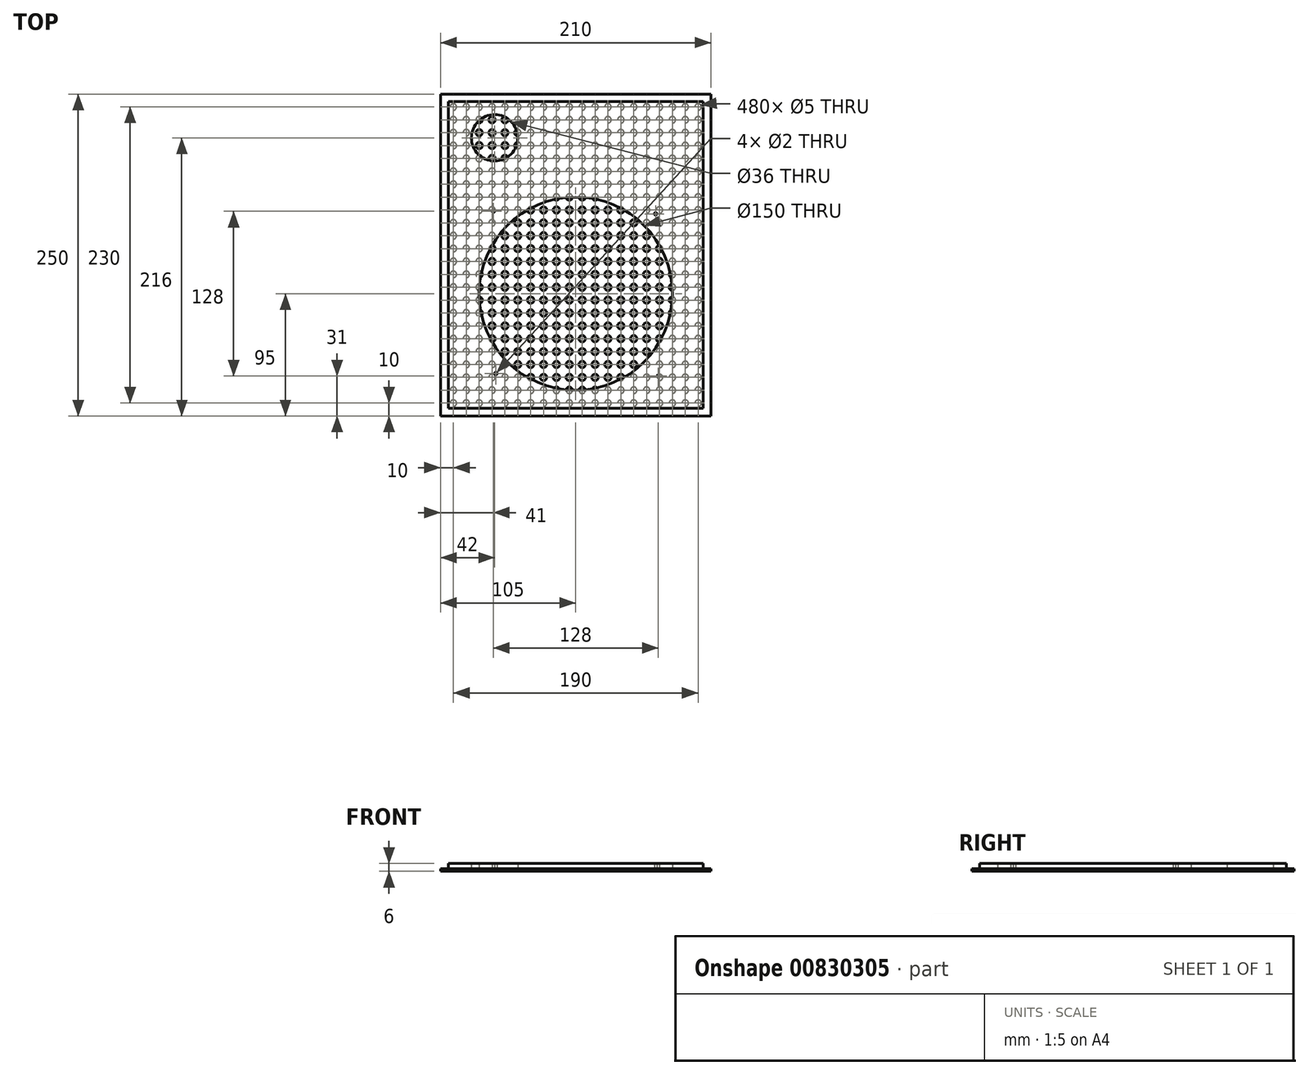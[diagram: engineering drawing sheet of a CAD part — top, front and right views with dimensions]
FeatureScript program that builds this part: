
annotation { "Feature Type Name" : "Feature", "Feature Type Description" : "" }
export const myFeature = defineFeature(function(context is Context, id is Id, definition is map)
    precondition{}
    {
        {
            var Q0;
            Q0=qCreatedBy(makeId("Top.planeOp"),FACE);
            var sketch = newSketch(context, id + "F0", { "sketchPlane" : qUnion([Q0])});
            skLineSegment(sketch, "E0.bottom", {"start": v(99, 119) * mm, "end": v(-99, 119) * mm});
            skLineSegment(sketch, "E0.top", {"start": v(99, -119) * mm, "end": v(-99, -119) * mm});
            skLineSegment(sketch, "E0.left", {"start": v(99, 119) * mm, "end": v(99, -119) * mm});
            skLineSegment(sketch, "E0.right", {"start": v(-99, 119) * mm, "end": v(-99, -119) * mm});
            skPoint(sketch, "E0.middle", {"position": v(0, 0) * mm});
            skSolve(sketch);
        }
        {
            var Q0;
            Q0=makeQuery(id+"F0.imprint","IMPRINT",FACE,{"disambiguationData":[TD([[makeQuery(id+"F0.imprint","IMPRINT",EDGE,{"derivedFrom":sQuery(id+"F0.wireOp",EDGE,"E0.bottom")}),1.0]])]});
            var sketch = newSketch(context, id + "F1", { "sketchPlane" : qUnion([Q0])});
            skCircle(sketch, "E1", {"center": v(0, -30) * mm, "radius": 75 * mm});
            skCircle(sketch, "E2", {"center": v(-63, 91) * mm, "radius": 18 * mm});
            skCircle(sketch, "E3", {"center": v(-64, 34) * mm, "radius": 1 * mm});
            skCircle(sketch, "E4", {"center": v(61.98, 31.98) * mm, "radius": 1 * mm});
            skCircle(sketch, "E5", {"center": v(64, -94) * mm, "radius": 1 * mm});
            skCircle(sketch, "E6", {"center": v(-61.98, -91.98) * mm, "radius": 1 * mm});
            skSolve(sketch);
        }
        {
            var Q0;
            Q0=qCreatedBy(makeId("Top.planeOp"),FACE);
            var sketch = newSketch(context, id + "F2", { "sketchPlane" : qUnion([Q0])});
            skLineSegment(sketch, "E7.bottom", {"start": v(-105, 125) * mm, "end": v(105, 125) * mm});
            skLineSegment(sketch, "E7.top", {"start": v(-105, -125) * mm, "end": v(105, -125) * mm});
            skLineSegment(sketch, "E7.left", {"start": v(-105, 125) * mm, "end": v(-105, -125) * mm});
            skLineSegment(sketch, "E7.right", {"start": v(105, 125) * mm, "end": v(105, -125) * mm});
            skPoint(sketch, "E7.middle", {"position": v(0, 0) * mm});
            skCircle(sketch, "E8", {"center": v(95, -115) * mm, "radius": 2.5 * mm});
            skCircle(sketch, "E9.0.1.0", {"center": v(95, -105) * mm, "radius": 2.5 * mm});
            skCircle(sketch, "E9.0.2.0", {"center": v(95, -95) * mm, "radius": 2.5 * mm});
            skCircle(sketch, "E9.0.3.0", {"center": v(95, -85) * mm, "radius": 2.5 * mm});
            skCircle(sketch, "E9.0.4.0", {"center": v(95, -75) * mm, "radius": 2.5 * mm});
            skCircle(sketch, "E9.0.5.0", {"center": v(95, -65) * mm, "radius": 2.5 * mm});
            skCircle(sketch, "E9.0.6.0", {"center": v(95, -55) * mm, "radius": 2.5 * mm});
            skCircle(sketch, "E9.0.7.0", {"center": v(95, -45) * mm, "radius": 2.5 * mm});
            skCircle(sketch, "E9.0.8.0", {"center": v(95, -35) * mm, "radius": 2.5 * mm});
            skCircle(sketch, "E9.0.9.0", {"center": v(95, -25) * mm, "radius": 2.5 * mm});
            skCircle(sketch, "E9.0.10.0", {"center": v(95, -15) * mm, "radius": 2.5 * mm});
            skCircle(sketch, "E9.0.11.0", {"center": v(95, -5) * mm, "radius": 2.5 * mm});
            skCircle(sketch, "E9.0.12.0", {"center": v(95, 5) * mm, "radius": 2.5 * mm});
            skCircle(sketch, "E9.0.13.0", {"center": v(95, 15) * mm, "radius": 2.5 * mm});
            skCircle(sketch, "E9.0.14.0", {"center": v(95, 25) * mm, "radius": 2.5 * mm});
            skCircle(sketch, "E9.0.15.0", {"center": v(95, 35) * mm, "radius": 2.5 * mm});
            skCircle(sketch, "E9.0.16.0", {"center": v(95, 45) * mm, "radius": 2.5 * mm});
            skCircle(sketch, "E9.0.17.0", {"center": v(95, 55) * mm, "radius": 2.5 * mm});
            skCircle(sketch, "E9.0.18.0", {"center": v(95, 65) * mm, "radius": 2.5 * mm});
            skCircle(sketch, "E9.0.19.0", {"center": v(95, 75) * mm, "radius": 2.5 * mm});
            skCircle(sketch, "E9.0.20.0", {"center": v(95, 85) * mm, "radius": 2.5 * mm});
            skCircle(sketch, "E9.0.21.0", {"center": v(95, 95) * mm, "radius": 2.5 * mm});
            skCircle(sketch, "E9.0.22.0", {"center": v(95, 105) * mm, "radius": 2.5 * mm});
            skCircle(sketch, "E9.0.23.0", {"center": v(95, 115) * mm, "radius": 2.5 * mm});
            skCircle(sketch, "E9.1.0.0", {"center": v(85, -115) * mm, "radius": 2.5 * mm});
            skCircle(sketch, "E9.1.1.0", {"center": v(85, -105) * mm, "radius": 2.5 * mm});
            skCircle(sketch, "E9.1.2.0", {"center": v(85, -95) * mm, "radius": 2.5 * mm});
            skCircle(sketch, "E9.1.3.0", {"center": v(85, -85) * mm, "radius": 2.5 * mm});
            skCircle(sketch, "E9.1.4.0", {"center": v(85, -75) * mm, "radius": 2.5 * mm});
            skCircle(sketch, "E9.1.5.0", {"center": v(85, -65) * mm, "radius": 2.5 * mm});
            skCircle(sketch, "E9.1.6.0", {"center": v(85, -55) * mm, "radius": 2.5 * mm});
            skCircle(sketch, "E9.1.7.0", {"center": v(85, -45) * mm, "radius": 2.5 * mm});
            skCircle(sketch, "E9.1.8.0", {"center": v(85, -35) * mm, "radius": 2.5 * mm});
            skCircle(sketch, "E9.1.9.0", {"center": v(85, -25) * mm, "radius": 2.5 * mm});
            skCircle(sketch, "E9.1.10.0", {"center": v(85, -15) * mm, "radius": 2.5 * mm});
            skCircle(sketch, "E9.1.11.0", {"center": v(85, -5) * mm, "radius": 2.5 * mm});
            skCircle(sketch, "E9.1.12.0", {"center": v(85, 5) * mm, "radius": 2.5 * mm});
            skCircle(sketch, "E9.1.13.0", {"center": v(85, 15) * mm, "radius": 2.5 * mm});
            skCircle(sketch, "E9.1.14.0", {"center": v(85, 25) * mm, "radius": 2.5 * mm});
            skCircle(sketch, "E9.1.15.0", {"center": v(85, 35) * mm, "radius": 2.5 * mm});
            skCircle(sketch, "E9.1.16.0", {"center": v(85, 45) * mm, "radius": 2.5 * mm});
            skCircle(sketch, "E9.1.17.0", {"center": v(85, 55) * mm, "radius": 2.5 * mm});
            skCircle(sketch, "E9.1.18.0", {"center": v(85, 65) * mm, "radius": 2.5 * mm});
            skCircle(sketch, "E9.1.19.0", {"center": v(85, 75) * mm, "radius": 2.5 * mm});
            skCircle(sketch, "E9.1.20.0", {"center": v(85, 85) * mm, "radius": 2.5 * mm});
            skCircle(sketch, "E9.1.21.0", {"center": v(85, 95) * mm, "radius": 2.5 * mm});
            skCircle(sketch, "E9.1.22.0", {"center": v(85, 105) * mm, "radius": 2.5 * mm});
            skCircle(sketch, "E9.1.23.0", {"center": v(85, 115) * mm, "radius": 2.5 * mm});
            skCircle(sketch, "E9.2.0.0", {"center": v(75, -115) * mm, "radius": 2.5 * mm});
            skCircle(sketch, "E9.2.1.0", {"center": v(75, -105) * mm, "radius": 2.5 * mm});
            skCircle(sketch, "E9.2.2.0", {"center": v(75, -95) * mm, "radius": 2.5 * mm});
            skCircle(sketch, "E9.2.3.0", {"center": v(75, -85) * mm, "radius": 2.5 * mm});
            skCircle(sketch, "E9.2.4.0", {"center": v(75, -75) * mm, "radius": 2.5 * mm});
            skCircle(sketch, "E9.2.5.0", {"center": v(75, -65) * mm, "radius": 2.5 * mm});
            skCircle(sketch, "E9.2.6.0", {"center": v(75, -55) * mm, "radius": 2.5 * mm});
            skCircle(sketch, "E9.2.7.0", {"center": v(75, -45) * mm, "radius": 2.5 * mm});
            skCircle(sketch, "E9.2.8.0", {"center": v(75, -35) * mm, "radius": 2.5 * mm});
            skCircle(sketch, "E9.2.9.0", {"center": v(75, -25) * mm, "radius": 2.5 * mm});
            skCircle(sketch, "E9.2.10.0", {"center": v(75, -15) * mm, "radius": 2.5 * mm});
            skCircle(sketch, "E9.2.11.0", {"center": v(75, -5) * mm, "radius": 2.5 * mm});
            skCircle(sketch, "E9.2.12.0", {"center": v(75, 5) * mm, "radius": 2.5 * mm});
            skCircle(sketch, "E9.2.13.0", {"center": v(75, 15) * mm, "radius": 2.5 * mm});
            skCircle(sketch, "E9.2.14.0", {"center": v(75, 25) * mm, "radius": 2.5 * mm});
            skCircle(sketch, "E9.2.15.0", {"center": v(75, 35) * mm, "radius": 2.5 * mm});
            skCircle(sketch, "E9.2.16.0", {"center": v(75, 45) * mm, "radius": 2.5 * mm});
            skCircle(sketch, "E9.2.17.0", {"center": v(75, 55) * mm, "radius": 2.5 * mm});
            skCircle(sketch, "E9.2.18.0", {"center": v(75, 65) * mm, "radius": 2.5 * mm});
            skCircle(sketch, "E9.2.19.0", {"center": v(75, 75) * mm, "radius": 2.5 * mm});
            skCircle(sketch, "E9.2.20.0", {"center": v(75, 85) * mm, "radius": 2.5 * mm});
            skCircle(sketch, "E9.2.21.0", {"center": v(75, 95) * mm, "radius": 2.5 * mm});
            skCircle(sketch, "E9.2.22.0", {"center": v(75, 105) * mm, "radius": 2.5 * mm});
            skCircle(sketch, "E9.2.23.0", {"center": v(75, 115) * mm, "radius": 2.5 * mm});
            skCircle(sketch, "E9.3.0.0", {"center": v(65, -115) * mm, "radius": 2.5 * mm});
            skCircle(sketch, "E9.3.1.0", {"center": v(65, -105) * mm, "radius": 2.5 * mm});
            skCircle(sketch, "E9.3.2.0", {"center": v(65, -95) * mm, "radius": 2.5 * mm});
            skCircle(sketch, "E9.3.3.0", {"center": v(65, -85) * mm, "radius": 2.5 * mm});
            skCircle(sketch, "E9.3.4.0", {"center": v(65, -75) * mm, "radius": 2.5 * mm});
            skCircle(sketch, "E9.3.5.0", {"center": v(65, -65) * mm, "radius": 2.5 * mm});
            skCircle(sketch, "E9.3.6.0", {"center": v(65, -55) * mm, "radius": 2.5 * mm});
            skCircle(sketch, "E9.3.7.0", {"center": v(65, -45) * mm, "radius": 2.5 * mm});
            skCircle(sketch, "E9.3.8.0", {"center": v(65, -35) * mm, "radius": 2.5 * mm});
            skCircle(sketch, "E9.3.9.0", {"center": v(65, -25) * mm, "radius": 2.5 * mm});
            skCircle(sketch, "E9.3.10.0", {"center": v(65, -15) * mm, "radius": 2.5 * mm});
            skCircle(sketch, "E9.3.11.0", {"center": v(65, -5) * mm, "radius": 2.5 * mm});
            skCircle(sketch, "E9.3.12.0", {"center": v(65, 5) * mm, "radius": 2.5 * mm});
            skCircle(sketch, "E9.3.13.0", {"center": v(65, 15) * mm, "radius": 2.5 * mm});
            skCircle(sketch, "E9.3.14.0", {"center": v(65, 25) * mm, "radius": 2.5 * mm});
            skCircle(sketch, "E9.3.15.0", {"center": v(65, 35) * mm, "radius": 2.5 * mm});
            skCircle(sketch, "E9.3.16.0", {"center": v(65, 45) * mm, "radius": 2.5 * mm});
            skCircle(sketch, "E9.3.17.0", {"center": v(65, 55) * mm, "radius": 2.5 * mm});
            skCircle(sketch, "E9.3.18.0", {"center": v(65, 65) * mm, "radius": 2.5 * mm});
            skCircle(sketch, "E9.3.19.0", {"center": v(65, 75) * mm, "radius": 2.5 * mm});
            skCircle(sketch, "E9.3.20.0", {"center": v(65, 85) * mm, "radius": 2.5 * mm});
            skCircle(sketch, "E9.3.21.0", {"center": v(65, 95) * mm, "radius": 2.5 * mm});
            skCircle(sketch, "E9.3.22.0", {"center": v(65, 105) * mm, "radius": 2.5 * mm});
            skCircle(sketch, "E9.3.23.0", {"center": v(65, 115) * mm, "radius": 2.5 * mm});
            skCircle(sketch, "E9.4.0.0", {"center": v(55, -115) * mm, "radius": 2.5 * mm});
            skCircle(sketch, "E9.4.1.0", {"center": v(55, -105) * mm, "radius": 2.5 * mm});
            skCircle(sketch, "E9.4.2.0", {"center": v(55, -95) * mm, "radius": 2.5 * mm});
            skCircle(sketch, "E9.4.3.0", {"center": v(55, -85) * mm, "radius": 2.5 * mm});
            skCircle(sketch, "E9.4.4.0", {"center": v(55, -75) * mm, "radius": 2.5 * mm});
            skCircle(sketch, "E9.4.5.0", {"center": v(55, -65) * mm, "radius": 2.5 * mm});
            skCircle(sketch, "E9.4.6.0", {"center": v(55, -55) * mm, "radius": 2.5 * mm});
            skCircle(sketch, "E9.4.7.0", {"center": v(55, -45) * mm, "radius": 2.5 * mm});
            skCircle(sketch, "E9.4.8.0", {"center": v(55, -35) * mm, "radius": 2.5 * mm});
            skCircle(sketch, "E9.4.9.0", {"center": v(55, -25) * mm, "radius": 2.5 * mm});
            skCircle(sketch, "E9.4.10.0", {"center": v(55, -15) * mm, "radius": 2.5 * mm});
            skCircle(sketch, "E9.4.11.0", {"center": v(55, -5) * mm, "radius": 2.5 * mm});
            skCircle(sketch, "E9.4.12.0", {"center": v(55, 5) * mm, "radius": 2.5 * mm});
            skCircle(sketch, "E9.4.13.0", {"center": v(55, 15) * mm, "radius": 2.5 * mm});
            skCircle(sketch, "E9.4.14.0", {"center": v(55, 25) * mm, "radius": 2.5 * mm});
            skCircle(sketch, "E9.4.15.0", {"center": v(55, 35) * mm, "radius": 2.5 * mm});
            skCircle(sketch, "E9.4.16.0", {"center": v(55, 45) * mm, "radius": 2.5 * mm});
            skCircle(sketch, "E9.4.17.0", {"center": v(55, 55) * mm, "radius": 2.5 * mm});
            skCircle(sketch, "E9.4.18.0", {"center": v(55, 65) * mm, "radius": 2.5 * mm});
            skCircle(sketch, "E9.4.19.0", {"center": v(55, 75) * mm, "radius": 2.5 * mm});
            skCircle(sketch, "E9.4.20.0", {"center": v(55, 85) * mm, "radius": 2.5 * mm});
            skCircle(sketch, "E9.4.21.0", {"center": v(55, 95) * mm, "radius": 2.5 * mm});
            skCircle(sketch, "E9.4.22.0", {"center": v(55, 105) * mm, "radius": 2.5 * mm});
            skCircle(sketch, "E9.4.23.0", {"center": v(55, 115) * mm, "radius": 2.5 * mm});
            skCircle(sketch, "E9.5.0.0", {"center": v(45, -115) * mm, "radius": 2.5 * mm});
            skCircle(sketch, "E9.5.1.0", {"center": v(45, -105) * mm, "radius": 2.5 * mm});
            skCircle(sketch, "E9.5.2.0", {"center": v(45, -95) * mm, "radius": 2.5 * mm});
            skCircle(sketch, "E9.5.3.0", {"center": v(45, -85) * mm, "radius": 2.5 * mm});
            skCircle(sketch, "E9.5.4.0", {"center": v(45, -75) * mm, "radius": 2.5 * mm});
            skCircle(sketch, "E9.5.5.0", {"center": v(45, -65) * mm, "radius": 2.5 * mm});
            skCircle(sketch, "E9.5.6.0", {"center": v(45, -55) * mm, "radius": 2.5 * mm});
            skCircle(sketch, "E9.5.7.0", {"center": v(45, -45) * mm, "radius": 2.5 * mm});
            skCircle(sketch, "E9.5.8.0", {"center": v(45, -35) * mm, "radius": 2.5 * mm});
            skCircle(sketch, "E9.5.9.0", {"center": v(45, -25) * mm, "radius": 2.5 * mm});
            skCircle(sketch, "E9.5.10.0", {"center": v(45, -15) * mm, "radius": 2.5 * mm});
            skCircle(sketch, "E9.5.11.0", {"center": v(45, -5) * mm, "radius": 2.5 * mm});
            skCircle(sketch, "E9.5.12.0", {"center": v(45, 5) * mm, "radius": 2.5 * mm});
            skCircle(sketch, "E9.5.13.0", {"center": v(45, 15) * mm, "radius": 2.5 * mm});
            skCircle(sketch, "E9.5.14.0", {"center": v(45, 25) * mm, "radius": 2.5 * mm});
            skCircle(sketch, "E9.5.15.0", {"center": v(45, 35) * mm, "radius": 2.5 * mm});
            skCircle(sketch, "E9.5.16.0", {"center": v(45, 45) * mm, "radius": 2.5 * mm});
            skCircle(sketch, "E9.5.17.0", {"center": v(45, 55) * mm, "radius": 2.5 * mm});
            skCircle(sketch, "E9.5.18.0", {"center": v(45, 65) * mm, "radius": 2.5 * mm});
            skCircle(sketch, "E9.5.19.0", {"center": v(45, 75) * mm, "radius": 2.5 * mm});
            skCircle(sketch, "E9.5.20.0", {"center": v(45, 85) * mm, "radius": 2.5 * mm});
            skCircle(sketch, "E9.5.21.0", {"center": v(45, 95) * mm, "radius": 2.5 * mm});
            skCircle(sketch, "E9.5.22.0", {"center": v(45, 105) * mm, "radius": 2.5 * mm});
            skCircle(sketch, "E9.5.23.0", {"center": v(45, 115) * mm, "radius": 2.5 * mm});
            skCircle(sketch, "E9.6.0.0", {"center": v(35, -115) * mm, "radius": 2.5 * mm});
            skCircle(sketch, "E9.6.1.0", {"center": v(35, -105) * mm, "radius": 2.5 * mm});
            skCircle(sketch, "E9.6.2.0", {"center": v(35, -95) * mm, "radius": 2.5 * mm});
            skCircle(sketch, "E9.6.3.0", {"center": v(35, -85) * mm, "radius": 2.5 * mm});
            skCircle(sketch, "E9.6.4.0", {"center": v(35, -75) * mm, "radius": 2.5 * mm});
            skCircle(sketch, "E9.6.5.0", {"center": v(35, -65) * mm, "radius": 2.5 * mm});
            skCircle(sketch, "E9.6.6.0", {"center": v(35, -55) * mm, "radius": 2.5 * mm});
            skCircle(sketch, "E9.6.7.0", {"center": v(35, -45) * mm, "radius": 2.5 * mm});
            skCircle(sketch, "E9.6.8.0", {"center": v(35, -35) * mm, "radius": 2.5 * mm});
            skCircle(sketch, "E9.6.9.0", {"center": v(35, -25) * mm, "radius": 2.5 * mm});
            skCircle(sketch, "E9.6.10.0", {"center": v(35, -15) * mm, "radius": 2.5 * mm});
            skCircle(sketch, "E9.6.11.0", {"center": v(35, -5) * mm, "radius": 2.5 * mm});
            skCircle(sketch, "E9.6.12.0", {"center": v(35, 5) * mm, "radius": 2.5 * mm});
            skCircle(sketch, "E9.6.13.0", {"center": v(35, 15) * mm, "radius": 2.5 * mm});
            skCircle(sketch, "E9.6.14.0", {"center": v(35, 25) * mm, "radius": 2.5 * mm});
            skCircle(sketch, "E9.6.15.0", {"center": v(35, 35) * mm, "radius": 2.5 * mm});
            skCircle(sketch, "E9.6.16.0", {"center": v(35, 45) * mm, "radius": 2.5 * mm});
            skCircle(sketch, "E9.6.17.0", {"center": v(35, 55) * mm, "radius": 2.5 * mm});
            skCircle(sketch, "E9.6.18.0", {"center": v(35, 65) * mm, "radius": 2.5 * mm});
            skCircle(sketch, "E9.6.19.0", {"center": v(35, 75) * mm, "radius": 2.5 * mm});
            skCircle(sketch, "E9.6.20.0", {"center": v(35, 85) * mm, "radius": 2.5 * mm});
            skCircle(sketch, "E9.6.21.0", {"center": v(35, 95) * mm, "radius": 2.5 * mm});
            skCircle(sketch, "E9.6.22.0", {"center": v(35, 105) * mm, "radius": 2.5 * mm});
            skCircle(sketch, "E9.6.23.0", {"center": v(35, 115) * mm, "radius": 2.5 * mm});
            skCircle(sketch, "E9.7.0.0", {"center": v(25, -115) * mm, "radius": 2.5 * mm});
            skCircle(sketch, "E9.7.1.0", {"center": v(25, -105) * mm, "radius": 2.5 * mm});
            skCircle(sketch, "E9.7.2.0", {"center": v(25, -95) * mm, "radius": 2.5 * mm});
            skCircle(sketch, "E9.7.3.0", {"center": v(25, -85) * mm, "radius": 2.5 * mm});
            skCircle(sketch, "E9.7.4.0", {"center": v(25, -75) * mm, "radius": 2.5 * mm});
            skCircle(sketch, "E9.7.5.0", {"center": v(25, -65) * mm, "radius": 2.5 * mm});
            skCircle(sketch, "E9.7.6.0", {"center": v(25, -55) * mm, "radius": 2.5 * mm});
            skCircle(sketch, "E9.7.7.0", {"center": v(25, -45) * mm, "radius": 2.5 * mm});
            skCircle(sketch, "E9.7.8.0", {"center": v(25, -35) * mm, "radius": 2.5 * mm});
            skCircle(sketch, "E9.7.9.0", {"center": v(25, -25) * mm, "radius": 2.5 * mm});
            skCircle(sketch, "E9.7.10.0", {"center": v(25, -15) * mm, "radius": 2.5 * mm});
            skCircle(sketch, "E9.7.11.0", {"center": v(25, -5) * mm, "radius": 2.5 * mm});
            skCircle(sketch, "E9.7.12.0", {"center": v(25, 5) * mm, "radius": 2.5 * mm});
            skCircle(sketch, "E9.7.13.0", {"center": v(25, 15) * mm, "radius": 2.5 * mm});
            skCircle(sketch, "E9.7.14.0", {"center": v(25, 25) * mm, "radius": 2.5 * mm});
            skCircle(sketch, "E9.7.15.0", {"center": v(25, 35) * mm, "radius": 2.5 * mm});
            skCircle(sketch, "E9.7.16.0", {"center": v(25, 45) * mm, "radius": 2.5 * mm});
            skCircle(sketch, "E9.7.17.0", {"center": v(25, 55) * mm, "radius": 2.5 * mm});
            skCircle(sketch, "E9.7.18.0", {"center": v(25, 65) * mm, "radius": 2.5 * mm});
            skCircle(sketch, "E9.7.19.0", {"center": v(25, 75) * mm, "radius": 2.5 * mm});
            skCircle(sketch, "E9.7.20.0", {"center": v(25, 85) * mm, "radius": 2.5 * mm});
            skCircle(sketch, "E9.7.21.0", {"center": v(25, 95) * mm, "radius": 2.5 * mm});
            skCircle(sketch, "E9.7.22.0", {"center": v(25, 105) * mm, "radius": 2.5 * mm});
            skCircle(sketch, "E9.7.23.0", {"center": v(25, 115) * mm, "radius": 2.5 * mm});
            skCircle(sketch, "E9.8.0.0", {"center": v(15, -115) * mm, "radius": 2.5 * mm});
            skCircle(sketch, "E9.8.1.0", {"center": v(15, -105) * mm, "radius": 2.5 * mm});
            skCircle(sketch, "E9.8.2.0", {"center": v(15, -95) * mm, "radius": 2.5 * mm});
            skCircle(sketch, "E9.8.3.0", {"center": v(15, -85) * mm, "radius": 2.5 * mm});
            skCircle(sketch, "E9.8.4.0", {"center": v(15, -75) * mm, "radius": 2.5 * mm});
            skCircle(sketch, "E9.8.5.0", {"center": v(15, -65) * mm, "radius": 2.5 * mm});
            skCircle(sketch, "E9.8.6.0", {"center": v(15, -55) * mm, "radius": 2.5 * mm});
            skCircle(sketch, "E9.8.7.0", {"center": v(15, -45) * mm, "radius": 2.5 * mm});
            skCircle(sketch, "E9.8.8.0", {"center": v(15, -35) * mm, "radius": 2.5 * mm});
            skCircle(sketch, "E9.8.9.0", {"center": v(15, -25) * mm, "radius": 2.5 * mm});
            skCircle(sketch, "E9.8.10.0", {"center": v(15, -15) * mm, "radius": 2.5 * mm});
            skCircle(sketch, "E9.8.11.0", {"center": v(15, -5) * mm, "radius": 2.5 * mm});
            skCircle(sketch, "E9.8.12.0", {"center": v(15, 5) * mm, "radius": 2.5 * mm});
            skCircle(sketch, "E9.8.13.0", {"center": v(15, 15) * mm, "radius": 2.5 * mm});
            skCircle(sketch, "E9.8.14.0", {"center": v(15, 25) * mm, "radius": 2.5 * mm});
            skCircle(sketch, "E9.8.15.0", {"center": v(15, 35) * mm, "radius": 2.5 * mm});
            skCircle(sketch, "E9.8.16.0", {"center": v(15, 45) * mm, "radius": 2.5 * mm});
            skCircle(sketch, "E9.8.17.0", {"center": v(15, 55) * mm, "radius": 2.5 * mm});
            skCircle(sketch, "E9.8.18.0", {"center": v(15, 65) * mm, "radius": 2.5 * mm});
            skCircle(sketch, "E9.8.19.0", {"center": v(15, 75) * mm, "radius": 2.5 * mm});
            skCircle(sketch, "E9.8.20.0", {"center": v(15, 85) * mm, "radius": 2.5 * mm});
            skCircle(sketch, "E9.8.21.0", {"center": v(15, 95) * mm, "radius": 2.5 * mm});
            skCircle(sketch, "E9.8.22.0", {"center": v(15, 105) * mm, "radius": 2.5 * mm});
            skCircle(sketch, "E9.8.23.0", {"center": v(15, 115) * mm, "radius": 2.5 * mm});
            skCircle(sketch, "E9.9.0.0", {"center": v(5, -115) * mm, "radius": 2.5 * mm});
            skCircle(sketch, "E9.9.1.0", {"center": v(5, -105) * mm, "radius": 2.5 * mm});
            skCircle(sketch, "E9.9.2.0", {"center": v(5, -95) * mm, "radius": 2.5 * mm});
            skCircle(sketch, "E9.9.3.0", {"center": v(5, -85) * mm, "radius": 2.5 * mm});
            skCircle(sketch, "E9.9.4.0", {"center": v(5, -75) * mm, "radius": 2.5 * mm});
            skCircle(sketch, "E9.9.5.0", {"center": v(5, -65) * mm, "radius": 2.5 * mm});
            skCircle(sketch, "E9.9.6.0", {"center": v(5, -55) * mm, "radius": 2.5 * mm});
            skCircle(sketch, "E9.9.7.0", {"center": v(5, -45) * mm, "radius": 2.5 * mm});
            skCircle(sketch, "E9.9.8.0", {"center": v(5, -35) * mm, "radius": 2.5 * mm});
            skCircle(sketch, "E9.9.9.0", {"center": v(5, -25) * mm, "radius": 2.5 * mm});
            skCircle(sketch, "E9.9.10.0", {"center": v(5, -15) * mm, "radius": 2.5 * mm});
            skCircle(sketch, "E9.9.11.0", {"center": v(5, -5) * mm, "radius": 2.5 * mm});
            skCircle(sketch, "E9.9.12.0", {"center": v(5, 5) * mm, "radius": 2.5 * mm});
            skCircle(sketch, "E9.9.13.0", {"center": v(5, 15) * mm, "radius": 2.5 * mm});
            skCircle(sketch, "E9.9.14.0", {"center": v(5, 25) * mm, "radius": 2.5 * mm});
            skCircle(sketch, "E9.9.15.0", {"center": v(5, 35) * mm, "radius": 2.5 * mm});
            skCircle(sketch, "E9.9.16.0", {"center": v(5, 45) * mm, "radius": 2.5 * mm});
            skCircle(sketch, "E9.9.17.0", {"center": v(5, 55) * mm, "radius": 2.5 * mm});
            skCircle(sketch, "E9.9.18.0", {"center": v(5, 65) * mm, "radius": 2.5 * mm});
            skCircle(sketch, "E9.9.19.0", {"center": v(5, 75) * mm, "radius": 2.5 * mm});
            skCircle(sketch, "E9.9.20.0", {"center": v(5, 85) * mm, "radius": 2.5 * mm});
            skCircle(sketch, "E9.9.21.0", {"center": v(5, 95) * mm, "radius": 2.5 * mm});
            skCircle(sketch, "E9.9.22.0", {"center": v(5, 105) * mm, "radius": 2.5 * mm});
            skCircle(sketch, "E9.9.23.0", {"center": v(5, 115) * mm, "radius": 2.5 * mm});
            skCircle(sketch, "E9.10.0.0", {"center": v(-5, -115) * mm, "radius": 2.5 * mm});
            skCircle(sketch, "E9.10.1.0", {"center": v(-5, -105) * mm, "radius": 2.5 * mm});
            skCircle(sketch, "E9.10.2.0", {"center": v(-5, -95) * mm, "radius": 2.5 * mm});
            skCircle(sketch, "E9.10.3.0", {"center": v(-5, -85) * mm, "radius": 2.5 * mm});
            skCircle(sketch, "E9.10.4.0", {"center": v(-5, -75) * mm, "radius": 2.5 * mm});
            skCircle(sketch, "E9.10.5.0", {"center": v(-5, -65) * mm, "radius": 2.5 * mm});
            skCircle(sketch, "E9.10.6.0", {"center": v(-5, -55) * mm, "radius": 2.5 * mm});
            skCircle(sketch, "E9.10.7.0", {"center": v(-5, -45) * mm, "radius": 2.5 * mm});
            skCircle(sketch, "E9.10.8.0", {"center": v(-5, -35) * mm, "radius": 2.5 * mm});
            skCircle(sketch, "E9.10.9.0", {"center": v(-5, -25) * mm, "radius": 2.5 * mm});
            skCircle(sketch, "E9.10.10.0", {"center": v(-5, -15) * mm, "radius": 2.5 * mm});
            skCircle(sketch, "E9.10.11.0", {"center": v(-5, -5) * mm, "radius": 2.5 * mm});
            skCircle(sketch, "E9.10.12.0", {"center": v(-5, 5) * mm, "radius": 2.5 * mm});
            skCircle(sketch, "E9.10.13.0", {"center": v(-5, 15) * mm, "radius": 2.5 * mm});
            skCircle(sketch, "E9.10.14.0", {"center": v(-5, 25) * mm, "radius": 2.5 * mm});
            skCircle(sketch, "E9.10.15.0", {"center": v(-5, 35) * mm, "radius": 2.5 * mm});
            skCircle(sketch, "E9.10.16.0", {"center": v(-5, 45) * mm, "radius": 2.5 * mm});
            skCircle(sketch, "E9.10.17.0", {"center": v(-5, 55) * mm, "radius": 2.5 * mm});
            skCircle(sketch, "E9.10.18.0", {"center": v(-5, 65) * mm, "radius": 2.5 * mm});
            skCircle(sketch, "E9.10.19.0", {"center": v(-5, 75) * mm, "radius": 2.5 * mm});
            skCircle(sketch, "E9.10.20.0", {"center": v(-5, 85) * mm, "radius": 2.5 * mm});
            skCircle(sketch, "E9.10.21.0", {"center": v(-5, 95) * mm, "radius": 2.5 * mm});
            skCircle(sketch, "E9.10.22.0", {"center": v(-5, 105) * mm, "radius": 2.5 * mm});
            skCircle(sketch, "E9.10.23.0", {"center": v(-5, 115) * mm, "radius": 2.5 * mm});
            skCircle(sketch, "E9.11.0.0", {"center": v(-15, -115) * mm, "radius": 2.5 * mm});
            skCircle(sketch, "E9.11.1.0", {"center": v(-15, -105) * mm, "radius": 2.5 * mm});
            skCircle(sketch, "E9.11.2.0", {"center": v(-15, -95) * mm, "radius": 2.5 * mm});
            skCircle(sketch, "E9.11.3.0", {"center": v(-15, -85) * mm, "radius": 2.5 * mm});
            skCircle(sketch, "E9.11.4.0", {"center": v(-15, -75) * mm, "radius": 2.5 * mm});
            skCircle(sketch, "E9.11.5.0", {"center": v(-15, -65) * mm, "radius": 2.5 * mm});
            skCircle(sketch, "E9.11.6.0", {"center": v(-15, -55) * mm, "radius": 2.5 * mm});
            skCircle(sketch, "E9.11.7.0", {"center": v(-15, -45) * mm, "radius": 2.5 * mm});
            skCircle(sketch, "E9.11.8.0", {"center": v(-15, -35) * mm, "radius": 2.5 * mm});
            skCircle(sketch, "E9.11.9.0", {"center": v(-15, -25) * mm, "radius": 2.5 * mm});
            skCircle(sketch, "E9.11.10.0", {"center": v(-15, -15) * mm, "radius": 2.5 * mm});
            skCircle(sketch, "E9.11.11.0", {"center": v(-15, -5) * mm, "radius": 2.5 * mm});
            skCircle(sketch, "E9.11.12.0", {"center": v(-15, 5) * mm, "radius": 2.5 * mm});
            skCircle(sketch, "E9.11.13.0", {"center": v(-15, 15) * mm, "radius": 2.5 * mm});
            skCircle(sketch, "E9.11.14.0", {"center": v(-15, 25) * mm, "radius": 2.5 * mm});
            skCircle(sketch, "E9.11.15.0", {"center": v(-15, 35) * mm, "radius": 2.5 * mm});
            skCircle(sketch, "E9.11.16.0", {"center": v(-15, 45) * mm, "radius": 2.5 * mm});
            skCircle(sketch, "E9.11.17.0", {"center": v(-15, 55) * mm, "radius": 2.5 * mm});
            skCircle(sketch, "E9.11.18.0", {"center": v(-15, 65) * mm, "radius": 2.5 * mm});
            skCircle(sketch, "E9.11.19.0", {"center": v(-15, 75) * mm, "radius": 2.5 * mm});
            skCircle(sketch, "E9.11.20.0", {"center": v(-15, 85) * mm, "radius": 2.5 * mm});
            skCircle(sketch, "E9.11.21.0", {"center": v(-15, 95) * mm, "radius": 2.5 * mm});
            skCircle(sketch, "E9.11.22.0", {"center": v(-15, 105) * mm, "radius": 2.5 * mm});
            skCircle(sketch, "E9.11.23.0", {"center": v(-15, 115) * mm, "radius": 2.5 * mm});
            skCircle(sketch, "E9.12.0.0", {"center": v(-25, -115) * mm, "radius": 2.5 * mm});
            skCircle(sketch, "E9.12.1.0", {"center": v(-25, -105) * mm, "radius": 2.5 * mm});
            skCircle(sketch, "E9.12.2.0", {"center": v(-25, -95) * mm, "radius": 2.5 * mm});
            skCircle(sketch, "E9.12.3.0", {"center": v(-25, -85) * mm, "radius": 2.5 * mm});
            skCircle(sketch, "E9.12.4.0", {"center": v(-25, -75) * mm, "radius": 2.5 * mm});
            skCircle(sketch, "E9.12.5.0", {"center": v(-25, -65) * mm, "radius": 2.5 * mm});
            skCircle(sketch, "E9.12.6.0", {"center": v(-25, -55) * mm, "radius": 2.5 * mm});
            skCircle(sketch, "E9.12.7.0", {"center": v(-25, -45) * mm, "radius": 2.5 * mm});
            skCircle(sketch, "E9.12.8.0", {"center": v(-25, -35) * mm, "radius": 2.5 * mm});
            skCircle(sketch, "E9.12.9.0", {"center": v(-25, -25) * mm, "radius": 2.5 * mm});
            skCircle(sketch, "E9.12.10.0", {"center": v(-25, -15) * mm, "radius": 2.5 * mm});
            skCircle(sketch, "E9.12.11.0", {"center": v(-25, -5) * mm, "radius": 2.5 * mm});
            skCircle(sketch, "E9.12.12.0", {"center": v(-25, 5) * mm, "radius": 2.5 * mm});
            skCircle(sketch, "E9.12.13.0", {"center": v(-25, 15) * mm, "radius": 2.5 * mm});
            skCircle(sketch, "E9.12.14.0", {"center": v(-25, 25) * mm, "radius": 2.5 * mm});
            skCircle(sketch, "E9.12.15.0", {"center": v(-25, 35) * mm, "radius": 2.5 * mm});
            skCircle(sketch, "E9.12.16.0", {"center": v(-25, 45) * mm, "radius": 2.5 * mm});
            skCircle(sketch, "E9.12.17.0", {"center": v(-25, 55) * mm, "radius": 2.5 * mm});
            skCircle(sketch, "E9.12.18.0", {"center": v(-25, 65) * mm, "radius": 2.5 * mm});
            skCircle(sketch, "E9.12.19.0", {"center": v(-25, 75) * mm, "radius": 2.5 * mm});
            skCircle(sketch, "E9.12.20.0", {"center": v(-25, 85) * mm, "radius": 2.5 * mm});
            skCircle(sketch, "E9.12.21.0", {"center": v(-25, 95) * mm, "radius": 2.5 * mm});
            skCircle(sketch, "E9.12.22.0", {"center": v(-25, 105) * mm, "radius": 2.5 * mm});
            skCircle(sketch, "E9.12.23.0", {"center": v(-25, 115) * mm, "radius": 2.5 * mm});
            skCircle(sketch, "E9.13.0.0", {"center": v(-35, -115) * mm, "radius": 2.5 * mm});
            skCircle(sketch, "E9.13.1.0", {"center": v(-35, -105) * mm, "radius": 2.5 * mm});
            skCircle(sketch, "E9.13.2.0", {"center": v(-35, -95) * mm, "radius": 2.5 * mm});
            skCircle(sketch, "E9.13.3.0", {"center": v(-35, -85) * mm, "radius": 2.5 * mm});
            skCircle(sketch, "E9.13.4.0", {"center": v(-35, -75) * mm, "radius": 2.5 * mm});
            skCircle(sketch, "E9.13.5.0", {"center": v(-35, -65) * mm, "radius": 2.5 * mm});
            skCircle(sketch, "E9.13.6.0", {"center": v(-35, -55) * mm, "radius": 2.5 * mm});
            skCircle(sketch, "E9.13.7.0", {"center": v(-35, -45) * mm, "radius": 2.5 * mm});
            skCircle(sketch, "E9.13.8.0", {"center": v(-35, -35) * mm, "radius": 2.5 * mm});
            skCircle(sketch, "E9.13.9.0", {"center": v(-35, -25) * mm, "radius": 2.5 * mm});
            skCircle(sketch, "E9.13.10.0", {"center": v(-35, -15) * mm, "radius": 2.5 * mm});
            skCircle(sketch, "E9.13.11.0", {"center": v(-35, -5) * mm, "radius": 2.5 * mm});
            skCircle(sketch, "E9.13.12.0", {"center": v(-35, 5) * mm, "radius": 2.5 * mm});
            skCircle(sketch, "E9.13.13.0", {"center": v(-35, 15) * mm, "radius": 2.5 * mm});
            skCircle(sketch, "E9.13.14.0", {"center": v(-35, 25) * mm, "radius": 2.5 * mm});
            skCircle(sketch, "E9.13.15.0", {"center": v(-35, 35) * mm, "radius": 2.5 * mm});
            skCircle(sketch, "E9.13.16.0", {"center": v(-35, 45) * mm, "radius": 2.5 * mm});
            skCircle(sketch, "E9.13.17.0", {"center": v(-35, 55) * mm, "radius": 2.5 * mm});
            skCircle(sketch, "E9.13.18.0", {"center": v(-35, 65) * mm, "radius": 2.5 * mm});
            skCircle(sketch, "E9.13.19.0", {"center": v(-35, 75) * mm, "radius": 2.5 * mm});
            skCircle(sketch, "E9.13.20.0", {"center": v(-35, 85) * mm, "radius": 2.5 * mm});
            skCircle(sketch, "E9.13.21.0", {"center": v(-35, 95) * mm, "radius": 2.5 * mm});
            skCircle(sketch, "E9.13.22.0", {"center": v(-35, 105) * mm, "radius": 2.5 * mm});
            skCircle(sketch, "E9.13.23.0", {"center": v(-35, 115) * mm, "radius": 2.5 * mm});
            skCircle(sketch, "E9.14.0.0", {"center": v(-45, -115) * mm, "radius": 2.5 * mm});
            skCircle(sketch, "E9.14.1.0", {"center": v(-45, -105) * mm, "radius": 2.5 * mm});
            skCircle(sketch, "E9.14.2.0", {"center": v(-45, -95) * mm, "radius": 2.5 * mm});
            skCircle(sketch, "E9.14.3.0", {"center": v(-45, -85) * mm, "radius": 2.5 * mm});
            skCircle(sketch, "E9.14.4.0", {"center": v(-45, -75) * mm, "radius": 2.5 * mm});
            skCircle(sketch, "E9.14.5.0", {"center": v(-45, -65) * mm, "radius": 2.5 * mm});
            skCircle(sketch, "E9.14.6.0", {"center": v(-45, -55) * mm, "radius": 2.5 * mm});
            skCircle(sketch, "E9.14.7.0", {"center": v(-45, -45) * mm, "radius": 2.5 * mm});
            skCircle(sketch, "E9.14.8.0", {"center": v(-45, -35) * mm, "radius": 2.5 * mm});
            skCircle(sketch, "E9.14.9.0", {"center": v(-45, -25) * mm, "radius": 2.5 * mm});
            skCircle(sketch, "E9.14.10.0", {"center": v(-45, -15) * mm, "radius": 2.5 * mm});
            skCircle(sketch, "E9.14.11.0", {"center": v(-45, -5) * mm, "radius": 2.5 * mm});
            skCircle(sketch, "E9.14.12.0", {"center": v(-45, 5) * mm, "radius": 2.5 * mm});
            skCircle(sketch, "E9.14.13.0", {"center": v(-45, 15) * mm, "radius": 2.5 * mm});
            skCircle(sketch, "E9.14.14.0", {"center": v(-45, 25) * mm, "radius": 2.5 * mm});
            skCircle(sketch, "E9.14.15.0", {"center": v(-45, 35) * mm, "radius": 2.5 * mm});
            skCircle(sketch, "E9.14.16.0", {"center": v(-45, 45) * mm, "radius": 2.5 * mm});
            skCircle(sketch, "E9.14.17.0", {"center": v(-45, 55) * mm, "radius": 2.5 * mm});
            skCircle(sketch, "E9.14.18.0", {"center": v(-45, 65) * mm, "radius": 2.5 * mm});
            skCircle(sketch, "E9.14.19.0", {"center": v(-45, 75) * mm, "radius": 2.5 * mm});
            skCircle(sketch, "E9.14.20.0", {"center": v(-45, 85) * mm, "radius": 2.5 * mm});
            skCircle(sketch, "E9.14.21.0", {"center": v(-45, 95) * mm, "radius": 2.5 * mm});
            skCircle(sketch, "E9.14.22.0", {"center": v(-45, 105) * mm, "radius": 2.5 * mm});
            skCircle(sketch, "E9.14.23.0", {"center": v(-45, 115) * mm, "radius": 2.5 * mm});
            skCircle(sketch, "E9.15.0.0", {"center": v(-55, -115) * mm, "radius": 2.5 * mm});
            skCircle(sketch, "E9.15.1.0", {"center": v(-55, -105) * mm, "radius": 2.5 * mm});
            skCircle(sketch, "E9.15.2.0", {"center": v(-55, -95) * mm, "radius": 2.5 * mm});
            skCircle(sketch, "E9.15.3.0", {"center": v(-55, -85) * mm, "radius": 2.5 * mm});
            skCircle(sketch, "E9.15.4.0", {"center": v(-55, -75) * mm, "radius": 2.5 * mm});
            skCircle(sketch, "E9.15.5.0", {"center": v(-55, -65) * mm, "radius": 2.5 * mm});
            skCircle(sketch, "E9.15.6.0", {"center": v(-55, -55) * mm, "radius": 2.5 * mm});
            skCircle(sketch, "E9.15.7.0", {"center": v(-55, -45) * mm, "radius": 2.5 * mm});
            skCircle(sketch, "E9.15.8.0", {"center": v(-55, -35) * mm, "radius": 2.5 * mm});
            skCircle(sketch, "E9.15.9.0", {"center": v(-55, -25) * mm, "radius": 2.5 * mm});
            skCircle(sketch, "E9.15.10.0", {"center": v(-55, -15) * mm, "radius": 2.5 * mm});
            skCircle(sketch, "E9.15.11.0", {"center": v(-55, -5) * mm, "radius": 2.5 * mm});
            skCircle(sketch, "E9.15.12.0", {"center": v(-55, 5) * mm, "radius": 2.5 * mm});
            skCircle(sketch, "E9.15.13.0", {"center": v(-55, 15) * mm, "radius": 2.5 * mm});
            skCircle(sketch, "E9.15.14.0", {"center": v(-55, 25) * mm, "radius": 2.5 * mm});
            skCircle(sketch, "E9.15.15.0", {"center": v(-55, 35) * mm, "radius": 2.5 * mm});
            skCircle(sketch, "E9.15.16.0", {"center": v(-55, 45) * mm, "radius": 2.5 * mm});
            skCircle(sketch, "E9.15.17.0", {"center": v(-55, 55) * mm, "radius": 2.5 * mm});
            skCircle(sketch, "E9.15.18.0", {"center": v(-55, 65) * mm, "radius": 2.5 * mm});
            skCircle(sketch, "E9.15.19.0", {"center": v(-55, 75) * mm, "radius": 2.5 * mm});
            skCircle(sketch, "E9.15.20.0", {"center": v(-55, 85) * mm, "radius": 2.5 * mm});
            skCircle(sketch, "E9.15.21.0", {"center": v(-55, 95) * mm, "radius": 2.5 * mm});
            skCircle(sketch, "E9.15.22.0", {"center": v(-55, 105) * mm, "radius": 2.5 * mm});
            skCircle(sketch, "E9.15.23.0", {"center": v(-55, 115) * mm, "radius": 2.5 * mm});
            skCircle(sketch, "E9.16.0.0", {"center": v(-65, -115) * mm, "radius": 2.5 * mm});
            skCircle(sketch, "E9.16.1.0", {"center": v(-65, -105) * mm, "radius": 2.5 * mm});
            skCircle(sketch, "E9.16.2.0", {"center": v(-65, -95) * mm, "radius": 2.5 * mm});
            skCircle(sketch, "E9.16.3.0", {"center": v(-65, -85) * mm, "radius": 2.5 * mm});
            skCircle(sketch, "E9.16.4.0", {"center": v(-65, -75) * mm, "radius": 2.5 * mm});
            skCircle(sketch, "E9.16.5.0", {"center": v(-65, -65) * mm, "radius": 2.5 * mm});
            skCircle(sketch, "E9.16.6.0", {"center": v(-65, -55) * mm, "radius": 2.5 * mm});
            skCircle(sketch, "E9.16.7.0", {"center": v(-65, -45) * mm, "radius": 2.5 * mm});
            skCircle(sketch, "E9.16.8.0", {"center": v(-65, -35) * mm, "radius": 2.5 * mm});
            skCircle(sketch, "E9.16.9.0", {"center": v(-65, -25) * mm, "radius": 2.5 * mm});
            skCircle(sketch, "E9.16.10.0", {"center": v(-65, -15) * mm, "radius": 2.5 * mm});
            skCircle(sketch, "E9.16.11.0", {"center": v(-65, -5) * mm, "radius": 2.5 * mm});
            skCircle(sketch, "E9.16.12.0", {"center": v(-65, 5) * mm, "radius": 2.5 * mm});
            skCircle(sketch, "E9.16.13.0", {"center": v(-65, 15) * mm, "radius": 2.5 * mm});
            skCircle(sketch, "E9.16.14.0", {"center": v(-65, 25) * mm, "radius": 2.5 * mm});
            skCircle(sketch, "E9.16.15.0", {"center": v(-65, 35) * mm, "radius": 2.5 * mm});
            skCircle(sketch, "E9.16.16.0", {"center": v(-65, 45) * mm, "radius": 2.5 * mm});
            skCircle(sketch, "E9.16.17.0", {"center": v(-65, 55) * mm, "radius": 2.5 * mm});
            skCircle(sketch, "E9.16.18.0", {"center": v(-65, 65) * mm, "radius": 2.5 * mm});
            skCircle(sketch, "E9.16.19.0", {"center": v(-65, 75) * mm, "radius": 2.5 * mm});
            skCircle(sketch, "E9.16.20.0", {"center": v(-65, 85) * mm, "radius": 2.5 * mm});
            skCircle(sketch, "E9.16.21.0", {"center": v(-65, 95) * mm, "radius": 2.5 * mm});
            skCircle(sketch, "E9.16.22.0", {"center": v(-65, 105) * mm, "radius": 2.5 * mm});
            skCircle(sketch, "E9.16.23.0", {"center": v(-65, 115) * mm, "radius": 2.5 * mm});
            skCircle(sketch, "E9.17.0.0", {"center": v(-75, -115) * mm, "radius": 2.5 * mm});
            skCircle(sketch, "E9.17.1.0", {"center": v(-75, -105) * mm, "radius": 2.5 * mm});
            skCircle(sketch, "E9.17.2.0", {"center": v(-75, -95) * mm, "radius": 2.5 * mm});
            skCircle(sketch, "E9.17.3.0", {"center": v(-75, -85) * mm, "radius": 2.5 * mm});
            skCircle(sketch, "E9.17.4.0", {"center": v(-75, -75) * mm, "radius": 2.5 * mm});
            skCircle(sketch, "E9.17.5.0", {"center": v(-75, -65) * mm, "radius": 2.5 * mm});
            skCircle(sketch, "E9.17.6.0", {"center": v(-75, -55) * mm, "radius": 2.5 * mm});
            skCircle(sketch, "E9.17.7.0", {"center": v(-75, -45) * mm, "radius": 2.5 * mm});
            skCircle(sketch, "E9.17.8.0", {"center": v(-75, -35) * mm, "radius": 2.5 * mm});
            skCircle(sketch, "E9.17.9.0", {"center": v(-75, -25) * mm, "radius": 2.5 * mm});
            skCircle(sketch, "E9.17.10.0", {"center": v(-75, -15) * mm, "radius": 2.5 * mm});
            skCircle(sketch, "E9.17.11.0", {"center": v(-75, -5) * mm, "radius": 2.5 * mm});
            skCircle(sketch, "E9.17.12.0", {"center": v(-75, 5) * mm, "radius": 2.5 * mm});
            skCircle(sketch, "E9.17.13.0", {"center": v(-75, 15) * mm, "radius": 2.5 * mm});
            skCircle(sketch, "E9.17.14.0", {"center": v(-75, 25) * mm, "radius": 2.5 * mm});
            skCircle(sketch, "E9.17.15.0", {"center": v(-75, 35) * mm, "radius": 2.5 * mm});
            skCircle(sketch, "E9.17.16.0", {"center": v(-75, 45) * mm, "radius": 2.5 * mm});
            skCircle(sketch, "E9.17.17.0", {"center": v(-75, 55) * mm, "radius": 2.5 * mm});
            skCircle(sketch, "E9.17.18.0", {"center": v(-75, 65) * mm, "radius": 2.5 * mm});
            skCircle(sketch, "E9.17.19.0", {"center": v(-75, 75) * mm, "radius": 2.5 * mm});
            skCircle(sketch, "E9.17.20.0", {"center": v(-75, 85) * mm, "radius": 2.5 * mm});
            skCircle(sketch, "E9.17.21.0", {"center": v(-75, 95) * mm, "radius": 2.5 * mm});
            skCircle(sketch, "E9.17.22.0", {"center": v(-75, 105) * mm, "radius": 2.5 * mm});
            skCircle(sketch, "E9.17.23.0", {"center": v(-75, 115) * mm, "radius": 2.5 * mm});
            skCircle(sketch, "E9.18.0.0", {"center": v(-85, -115) * mm, "radius": 2.5 * mm});
            skCircle(sketch, "E9.18.1.0", {"center": v(-85, -105) * mm, "radius": 2.5 * mm});
            skCircle(sketch, "E9.18.2.0", {"center": v(-85, -95) * mm, "radius": 2.5 * mm});
            skCircle(sketch, "E9.18.3.0", {"center": v(-85, -85) * mm, "radius": 2.5 * mm});
            skCircle(sketch, "E9.18.4.0", {"center": v(-85, -75) * mm, "radius": 2.5 * mm});
            skCircle(sketch, "E9.18.5.0", {"center": v(-85, -65) * mm, "radius": 2.5 * mm});
            skCircle(sketch, "E9.18.6.0", {"center": v(-85, -55) * mm, "radius": 2.5 * mm});
            skCircle(sketch, "E9.18.7.0", {"center": v(-85, -45) * mm, "radius": 2.5 * mm});
            skCircle(sketch, "E9.18.8.0", {"center": v(-85, -35) * mm, "radius": 2.5 * mm});
            skCircle(sketch, "E9.18.9.0", {"center": v(-85, -25) * mm, "radius": 2.5 * mm});
            skCircle(sketch, "E9.18.10.0", {"center": v(-85, -15) * mm, "radius": 2.5 * mm});
            skCircle(sketch, "E9.18.11.0", {"center": v(-85, -5) * mm, "radius": 2.5 * mm});
            skCircle(sketch, "E9.18.12.0", {"center": v(-85, 5) * mm, "radius": 2.5 * mm});
            skCircle(sketch, "E9.18.13.0", {"center": v(-85, 15) * mm, "radius": 2.5 * mm});
            skCircle(sketch, "E9.18.14.0", {"center": v(-85, 25) * mm, "radius": 2.5 * mm});
            skCircle(sketch, "E9.18.15.0", {"center": v(-85, 35) * mm, "radius": 2.5 * mm});
            skCircle(sketch, "E9.18.16.0", {"center": v(-85, 45) * mm, "radius": 2.5 * mm});
            skCircle(sketch, "E9.18.17.0", {"center": v(-85, 55) * mm, "radius": 2.5 * mm});
            skCircle(sketch, "E9.18.18.0", {"center": v(-85, 65) * mm, "radius": 2.5 * mm});
            skCircle(sketch, "E9.18.19.0", {"center": v(-85, 75) * mm, "radius": 2.5 * mm});
            skCircle(sketch, "E9.18.20.0", {"center": v(-85, 85) * mm, "radius": 2.5 * mm});
            skCircle(sketch, "E9.18.21.0", {"center": v(-85, 95) * mm, "radius": 2.5 * mm});
            skCircle(sketch, "E9.18.22.0", {"center": v(-85, 105) * mm, "radius": 2.5 * mm});
            skCircle(sketch, "E9.18.23.0", {"center": v(-85, 115) * mm, "radius": 2.5 * mm});
            skCircle(sketch, "E9.19.0.0", {"center": v(-95, -115) * mm, "radius": 2.5 * mm});
            skCircle(sketch, "E9.19.1.0", {"center": v(-95, -105) * mm, "radius": 2.5 * mm});
            skCircle(sketch, "E9.19.2.0", {"center": v(-95, -95) * mm, "radius": 2.5 * mm});
            skCircle(sketch, "E9.19.3.0", {"center": v(-95, -85) * mm, "radius": 2.5 * mm});
            skCircle(sketch, "E9.19.4.0", {"center": v(-95, -75) * mm, "radius": 2.5 * mm});
            skCircle(sketch, "E9.19.5.0", {"center": v(-95, -65) * mm, "radius": 2.5 * mm});
            skCircle(sketch, "E9.19.6.0", {"center": v(-95, -55) * mm, "radius": 2.5 * mm});
            skCircle(sketch, "E9.19.7.0", {"center": v(-95, -45) * mm, "radius": 2.5 * mm});
            skCircle(sketch, "E9.19.8.0", {"center": v(-95, -35) * mm, "radius": 2.5 * mm});
            skCircle(sketch, "E9.19.9.0", {"center": v(-95, -25) * mm, "radius": 2.5 * mm});
            skCircle(sketch, "E9.19.10.0", {"center": v(-95, -15) * mm, "radius": 2.5 * mm});
            skCircle(sketch, "E9.19.11.0", {"center": v(-95, -5) * mm, "radius": 2.5 * mm});
            skCircle(sketch, "E9.19.12.0", {"center": v(-95, 5) * mm, "radius": 2.5 * mm});
            skCircle(sketch, "E9.19.13.0", {"center": v(-95, 15) * mm, "radius": 2.5 * mm});
            skCircle(sketch, "E9.19.14.0", {"center": v(-95, 25) * mm, "radius": 2.5 * mm});
            skCircle(sketch, "E9.19.15.0", {"center": v(-95, 35) * mm, "radius": 2.5 * mm});
            skCircle(sketch, "E9.19.16.0", {"center": v(-95, 45) * mm, "radius": 2.5 * mm});
            skCircle(sketch, "E9.19.17.0", {"center": v(-95, 55) * mm, "radius": 2.5 * mm});
            skCircle(sketch, "E9.19.18.0", {"center": v(-95, 65) * mm, "radius": 2.5 * mm});
            skCircle(sketch, "E9.19.19.0", {"center": v(-95, 75) * mm, "radius": 2.5 * mm});
            skCircle(sketch, "E9.19.20.0", {"center": v(-95, 85) * mm, "radius": 2.5 * mm});
            skCircle(sketch, "E9.19.21.0", {"center": v(-95, 95) * mm, "radius": 2.5 * mm});
            skCircle(sketch, "E9.19.22.0", {"center": v(-95, 105) * mm, "radius": 2.5 * mm});
            skCircle(sketch, "E9.19.23.0", {"center": v(-95, 115) * mm, "radius": 2.5 * mm});
            skLineSegment(sketch, "E9.direction1", {"start": v(95, -115) * mm, "end": v(85, -115) * mm, "construction": true});
            skLineSegment(sketch, "E9.direction2", {"start": v(95, -115) * mm, "end": v(95, -105) * mm, "construction": true});
            skSolve(sketch);
        }
        {
            var Q0;
            Q0=qSketchRegion(id+"F2",true);
            extrude(context, id + "F3", {"entities" : qUnion([Q0]), "depth" : 2 * mm, "offsetDistance" : 25 * mm});
        }
        {
            var Q0;
            Q0=makeQuery(id+"F1.imprint","IMPRINT",FACE,{"disambiguationData":[TD([[makeQuery(id+"F1.imprint","IMPRINT",EDGE,{"derivedFrom":sQuery(id+"F1.wireOp",EDGE,"E1")}),-1.0]])]});
            extrude(context, id + "F4", {"entities" : qUnion([Q0]), "depth" : 6 * mm, "offsetDistance" : 25 * mm});
        }
    });
